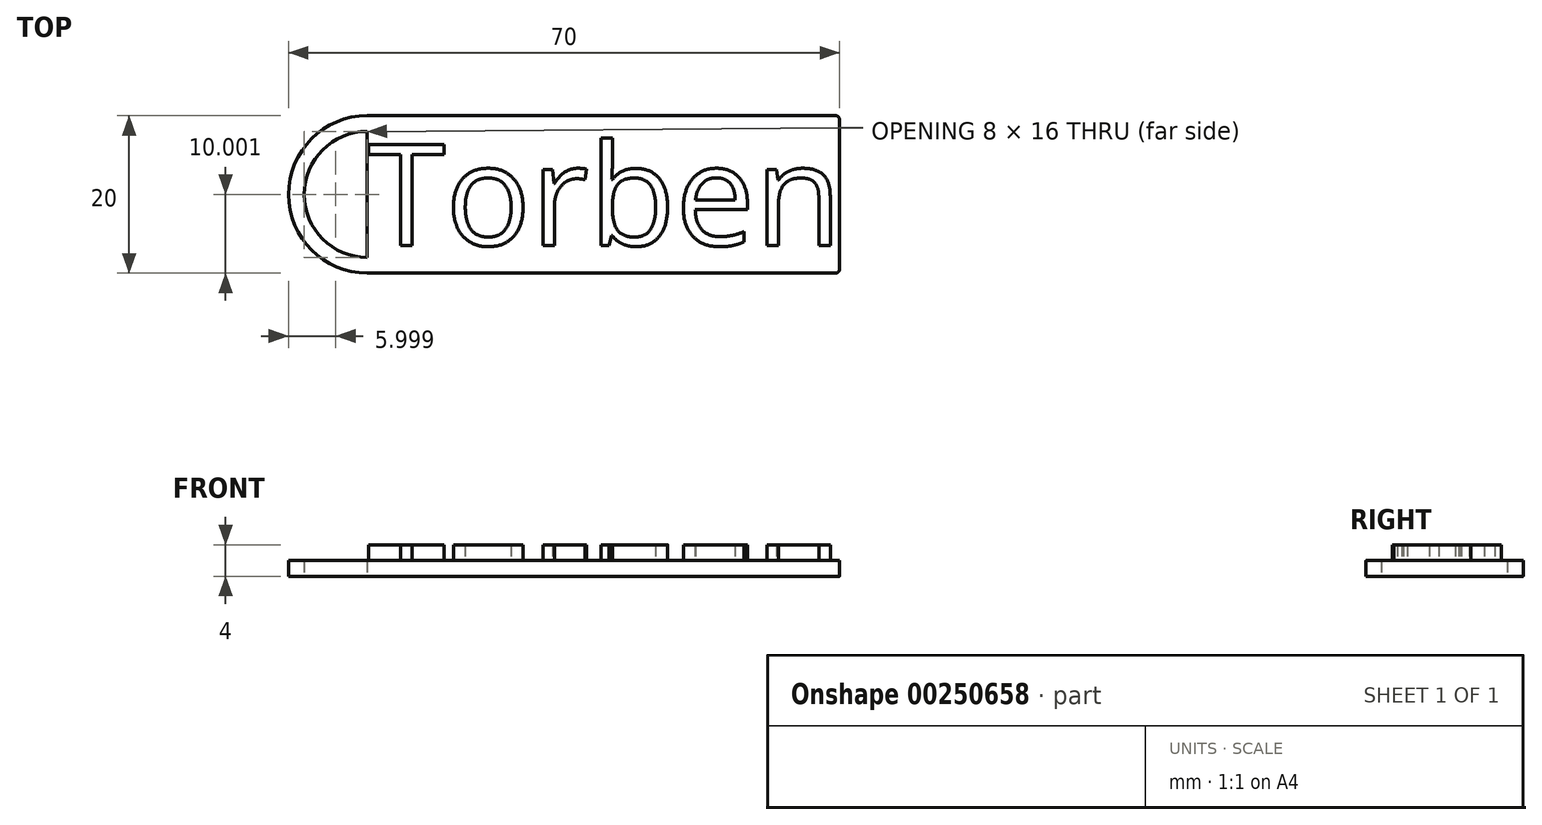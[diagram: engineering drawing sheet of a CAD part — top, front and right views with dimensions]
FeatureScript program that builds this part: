
annotation { "Feature Type Name" : "Feature", "Feature Type Description" : "" }
export const myFeature = defineFeature(function(context is Context, id is Id, definition is map)
    precondition{}
    {
        {
            var Q0;
            Q0=qCreatedBy(makeId("Top.planeOp"),FACE);
            var sketch = newSketch(context, id + "F0", { "sketchPlane" : qUnion([Q0])});
            skLineSegment(sketch, "E0.bottom", {"start": v(-5.27, 3.22) * mm, "end": v(54.73, 3.22) * mm});
            skLineSegment(sketch, "E0.top", {"start": v(-5.27, -16.78) * mm, "end": v(54.73, -16.78) * mm});
            skLineSegment(sketch, "E0.left", {"start": v(-5.27, 3.22) * mm, "end": v(-5.27, -16.78) * mm});
            skLineSegment(sketch, "E0.right", {"start": v(54.73, 3.22) * mm, "end": v(54.73, -16.78) * mm});
            skArc(sketch, "E1", {"start": v(-5.27, 3.22) * mm, "mid": v(-15.27, -6.78) * mm, "end": v(-5.27, -16.78) * mm});
            skArc(sketch, "E2", {"start": v(-5.27, 1.22) * mm, "mid": v(-13.27, -6.78) * mm, "end": v(-5.27, -14.78) * mm});
            skSolve(sketch);
        }
        {
            var Q0;
            Q0=qSketchRegion(id+"F0",true);
            extrude(context, id + "F4", {"entities" : qUnion([Q0]), "depth" : 2 * mm});
        }
        {
            var Q0;
            Q0=makeQuery(id+"F4.opExtrude","SWEPT_EDGE",EDGE,{"disambiguationData":[OSD([sQuery(id+"F0.wireOp",EDGE,"E0.top"),sQuery(id+"F0.wireOp",EDGE,"E0.right")])]});
            var Q1;
            Q1=makeQuery(id+"F4.opExtrude","SWEPT_EDGE",EDGE,{"disambiguationData":[OSD([sQuery(id+"F0.wireOp",EDGE,"E0.bottom"),sQuery(id+"F0.wireOp",EDGE,"E0.right")])]});
            fillet(context, id + "F1", {"entities" : qUnion([Q0, Q1]), "radius" : 0.5 * mm, "tangentPropagation" : true, "allowEdgeOverflow" : false});
        }
        {
            var Q0;
            Q0=makeQuery(id+"F4.opExtrude","CAP_FACE",FACE,{"disambiguationData":[OSD([sQuery(id+"F0.wireOp",EDGE,"E0.bottom"),sQuery(id+"F0.wireOp",EDGE,"E0.top"),sQuery(id+"F0.wireOp",EDGE,"E0.left"),sQuery(id+"F0.wireOp",EDGE,"E0.right"),sQuery(id+"F0.wireOp",EDGE,"E1"),sQuery(id+"F0.wireOp",EDGE,"E2")])],"isStart":false});
            var sketch = newSketch(context, id + "F2", { "sketchPlane" : qUnion([Q0])});
            skText(sketch, "E3", { "text": "Torben", "fontName": "OpenSans-Regular.ttf"});
            skPoint(sketch, "E4", {"position": v(-5.27, -6.78) * mm});
            const initialGuessF2  = {"E3": [-0.00527, -0.01325, 1, 0, 0.01294]};
            skSetInitialGuess(sketch, initialGuessF2);
            skSolve(sketch);
        }
        {
            var Q0;
            Q0 = qSketchRegion(id + "F2", true);
            extrude(context, id + "F3", {"entities" : qUnion([Q0]), "operationType" : NewBodyOperationType.ADD, "depth" : 2 * mm, "offsetDistance" : 25 * mm});
        }
    });
